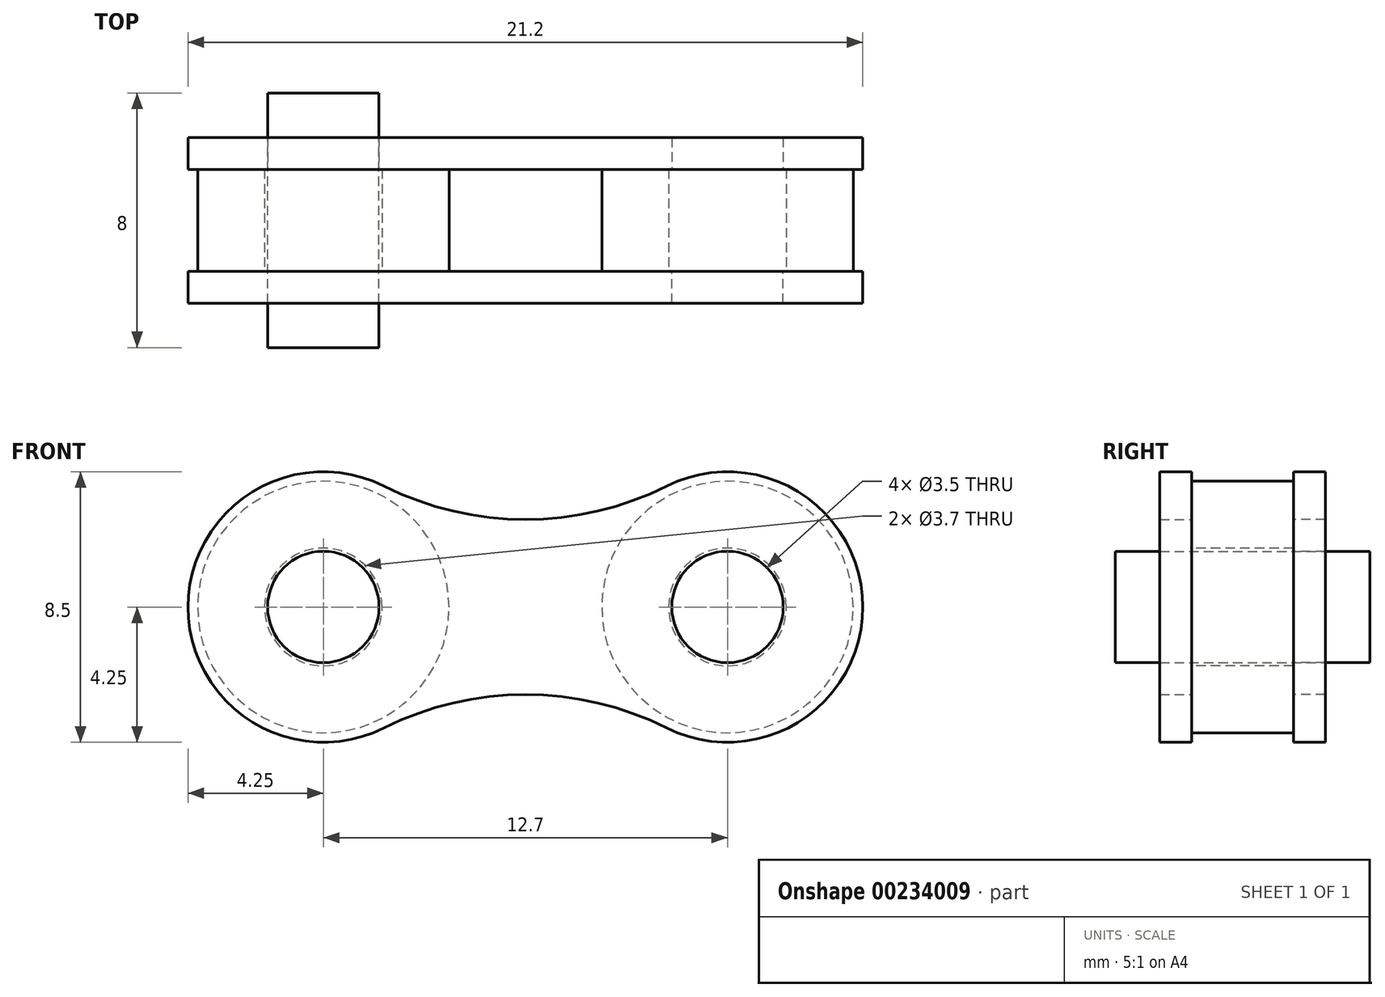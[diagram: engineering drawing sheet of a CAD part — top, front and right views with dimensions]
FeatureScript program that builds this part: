
annotation { "Feature Type Name" : "Feature", "Feature Type Description" : "" }
export const myFeature = defineFeature(function(context is Context, id is Id, definition is map)
    precondition{}
    {
        {
            var Q0;
            Q0=qCreatedBy(makeId("Front.planeOp"),FACE);
            var sketch = newSketch(context, id + "F0", { "sketchPlane" : qUnion([Q0])});
            skCircle(sketch, "E0", {"center": v(-6.35, 0) * mm, "radius": 3.95 * mm});
            skLineSegment(sketch, "E1", {"start": v(0, 6.67) * mm, "end": v(0, -6.2) * mm, "construction": true});
            skCircle(sketch, "E2.MirrorC", {"center": v(6.35, 0) * mm, "radius": 3.95 * mm});
            skCircle(sketch, "E3", {"center": v(-6.35, 0) * mm, "radius": 1.85 * mm});
            skCircle(sketch, "E4.MirrorC", {"center": v(6.35, 0) * mm, "radius": 1.85 * mm});
            skSolve(sketch);
        }
        {
            var Q0;
            Q0 = qSketchRegion(id + "F0", true);
            extrude(context, id + "F1", {"entities" : qUnion([Q0]), "endBound" : BoundingType.SYMMETRIC, "oppositeDirection" : true, "depth" : 3.2 * mm});
        }
        {
            var Q0;
            Q0=makeQuery(id+"F1.opExtrude","CAP_FACE",FACE,{"disambiguationData":[OSD([sQuery(id+"F0.wireOp",EDGE,"E0"),sQuery(id+"F0.wireOp",EDGE,"E3")])],"isStart":true});
            var sketch = newSketch(context, id + "F2", { "sketchPlane" : qUnion([Q0])});
            skCircle(sketch, "E5.0", {"center": v(-6.35, 0) * mm, "radius": 1.85 * mm, "construction": true});
            skArc(sketch, "E6", {"start": v(-4.45, 3.8) * mm, "mid": v(-10.6, 0) * mm, "end": v(-4.45, -3.8) * mm});
            skCircle(sketch, "E7", {"center": v(-6.35, 0) * mm, "radius": 1.75 * mm});
            skArc(sketch, "E8.MirrorC", {"start": v(4.45, 3.8) * mm, "mid": v(10.6, 0) * mm, "end": v(4.45, -3.8) * mm});
            skCircle(sketch, "E9.MirrorC", {"center": v(6.35, 0) * mm, "radius": 1.75 * mm});
            skArc(sketch, "E10", {"start": v(-4.45, 3.8) * mm, "mid": v(0, 2.75) * mm, "end": v(4.45, 3.8) * mm});
            skArc(sketch, "E11.MirrorCS", {"start": v(-4.45, -3.8) * mm, "mid": v(0, -2.75) * mm, "end": v(4.45, -3.8) * mm});
            skSolve(sketch);
        }
        {
            var Q0;
            Q0 = qSketchRegion(id + "F2", true);
            extrude(context, id + "F3", {"entities" : qUnion([Q0]), "depth" : 1 * mm});
        }
        {
            var Q0;
            Q0=makeQuery(id+"F3.opExtrude","SWEPT_BODY",BODY,{"disambiguationData":[OSD([sQuery(id+"F2.wireOp",EDGE,"E6"),sQuery(id+"F2.wireOp",EDGE,"E7"),sQuery(id+"F2.wireOp",EDGE,"E8.MirrorC"),sQuery(id+"F2.wireOp",EDGE,"E9.MirrorC"),sQuery(id+"F2.wireOp",EDGE,"E10"),sQuery(id+"F2.wireOp",EDGE,"E11.MirrorCS")])]});
            var Q1;
            Q1=qCreatedBy(makeId("Front.planeOp"),FACE);
            mirror(context, id + "F4", {"entities" : qUnion([Q0]), "mirrorPlane" : qUnion([Q1])});
        }
        {
            var Q0;
            Q0=qCreatedBy(makeId("Front.planeOp"),FACE);
            var sketch = newSketch(context, id + "F5", { "sketchPlane" : qUnion([Q0])});
            skCircle(sketch, "E12", {"center": v(-6.35, 0) * mm, "radius": 1.75 * mm});
            skSolve(sketch);
        }
        {
            var Q0;
            Q0 = qSketchRegion(id + "F5", true);
            extrude(context, id + "F6", {"entities" : qUnion([Q0]), "endBound" : BoundingType.SYMMETRIC, "depth" : 8 * mm});
        }
    });
